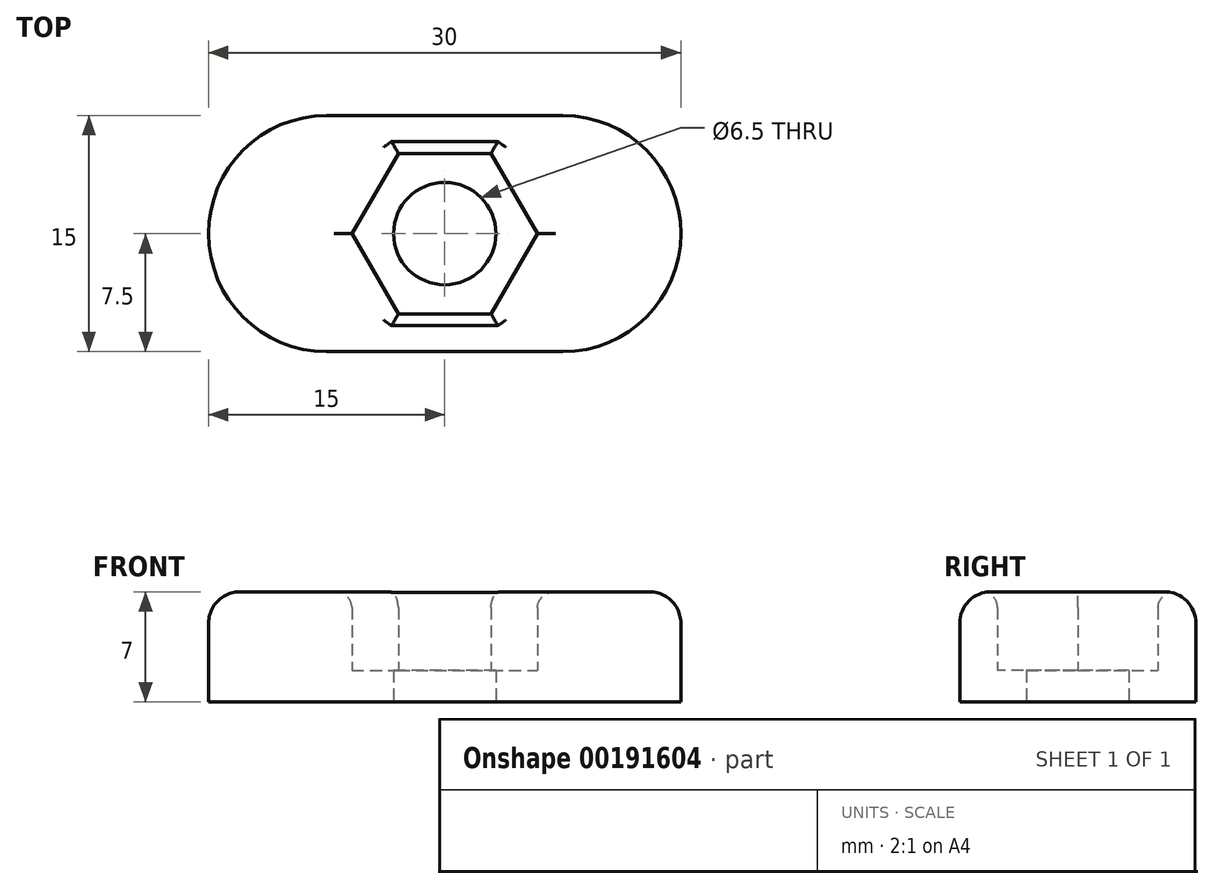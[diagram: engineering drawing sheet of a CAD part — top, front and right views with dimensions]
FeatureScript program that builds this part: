
annotation { "Feature Type Name" : "Feature", "Feature Type Description" : "" }
export const myFeature = defineFeature(function(context is Context, id is Id, definition is map)
    precondition{}
    {
        {
            var Q0;
            Q0=qCreatedBy(makeId("Top.planeOp"),FACE);
            var sketch = newSketch(context, id + "F0", { "sketchPlane" : qUnion([Q0])});
            skCircle(sketch, "E0.cCircle", {"center": v(0, 0) * mm, "radius": 5.1 * mm, "construction": true});
            skLineSegment(sketch, "E0.0", {"start": v(-2.94, 5.1) * mm, "end": v(2.94, 5.1) * mm});
            skLineSegment(sketch, "E0.1", {"start": v(2.94, 5.1) * mm, "end": v(5.89, 0) * mm});
            skLineSegment(sketch, "E0.2", {"start": v(5.89, 0) * mm, "end": v(2.94, -5.1) * mm});
            skLineSegment(sketch, "E0.3", {"start": v(2.94, -5.1) * mm, "end": v(-2.94, -5.1) * mm});
            skLineSegment(sketch, "E0.4", {"start": v(-2.94, -5.1) * mm, "end": v(-5.89, 0) * mm});
            skLineSegment(sketch, "E0.5", {"start": v(-5.89, 0) * mm, "end": v(-2.94, 5.1) * mm});
            skPoint(sketch, "E0.0.midPoint", {"position": v(0, 5.1) * mm});
            skLineSegment(sketch, "E1.bottom", {"start": v(-15, 7.5) * mm, "end": v(15, 7.5) * mm});
            skLineSegment(sketch, "E1.top", {"start": v(-15, -7.5) * mm, "end": v(15, -7.5) * mm});
            skLineSegment(sketch, "E1.left", {"start": v(-15, 7.5) * mm, "end": v(-15, -7.5) * mm});
            skLineSegment(sketch, "E1.right", {"start": v(15, 7.5) * mm, "end": v(15, -7.5) * mm});
            skCircle(sketch, "E2", {"center": v(0, 0) * mm, "radius": 3.25 * mm});
            skSolve(sketch);
        }
        {
            var Q0;
            Q0=makeQuery(id+"F0.imprint","IMPRINT",FACE,{"disambiguationData":[TD([[makeQuery(id+"F0.imprint","IMPRINT",EDGE,{"derivedFrom":sQuery(id+"F0.wireOp",EDGE,"E0.0")}),1.0]])]});
            extrude(context, id + "F1", {"entities" : qUnion([Q0]), "depth" : 7 * mm});
        }
        {
            var Q0;
            Q0=makeQuery(id+"F1.opExtrude","SWEPT_EDGE",EDGE,{"disambiguationData":[OSD([sQuery(id+"F0.wireOp",EDGE,"E1.top"),sQuery(id+"F0.wireOp",EDGE,"E1.left")])]});
            var Q1;
            Q1=makeQuery(id+"F1.opExtrude","SWEPT_EDGE",EDGE,{"disambiguationData":[OSD([sQuery(id+"F0.wireOp",EDGE,"E1.bottom"),sQuery(id+"F0.wireOp",EDGE,"E1.right")])]});
            var Q2;
            Q2=makeQuery(id+"F1.opExtrude","SWEPT_EDGE",EDGE,{"disambiguationData":[OSD([sQuery(id+"F0.wireOp",EDGE,"E1.bottom"),sQuery(id+"F0.wireOp",EDGE,"E1.left")])]});
            var Q3;
            Q3=makeQuery(id+"F1.opExtrude","SWEPT_EDGE",EDGE,{"disambiguationData":[OSD([sQuery(id+"F0.wireOp",EDGE,"E1.top"),sQuery(id+"F0.wireOp",EDGE,"E1.right")])]});
            fillet(context, id + "F2", {"entities" : qUnion([Q0, Q1, Q2, Q3]), "radius" : 7.5 * mm, "tangentPropagation" : true, "allowEdgeOverflow" : false});
        }
        {
            var Q0;
            {var subQ0=sQuery(id+"F0.wireOp",EDGE,"E1.right");var subQ1=sQuery(id+"F0.wireOp",EDGE,"E1.bottom");Q0=makeQuery(id+"F2.opFillet","BLEND_EDGE",EDGE,{"blendedFrom":[makeQuery(id+"F1.opExtrude","SWEPT_EDGE",EDGE,{"disambiguationData":[OSD([subQ1,subQ0])]}),makeQuery(id+"F1.opExtrude","CAP_FACE",FACE,{"disambiguationData":[OSD([sQuery(id+"F0.wireOp",EDGE,"E0.0"),sQuery(id+"F0.wireOp",EDGE,"E0.1"),sQuery(id+"F0.wireOp",EDGE,"E0.2"),sQuery(id+"F0.wireOp",EDGE,"E0.3"),sQuery(id+"F0.wireOp",EDGE,"E0.4"),sQuery(id+"F0.wireOp",EDGE,"E0.5"),subQ1,sQuery(id+"F0.wireOp",EDGE,"E1.top"),sQuery(id+"F0.wireOp",EDGE,"E1.left"),subQ0])],"isStart":false})],"blendedInto":[makeQuery(id+"F1.opExtrude","CAP_FACE",FACE,{"disambiguationData":[OSD([sQuery(id+"F0.wireOp",EDGE,"E0.0"),sQuery(id+"F0.wireOp",EDGE,"E0.1"),sQuery(id+"F0.wireOp",EDGE,"E0.2"),sQuery(id+"F0.wireOp",EDGE,"E0.3"),sQuery(id+"F0.wireOp",EDGE,"E0.4"),sQuery(id+"F0.wireOp",EDGE,"E0.5"),subQ1,sQuery(id+"F0.wireOp",EDGE,"E1.top"),sQuery(id+"F0.wireOp",EDGE,"E1.left"),subQ0])],"isStart":false})]});}
            fillet(context, id + "F3", {"entities" : qUnion([Q0]), "radius" : 2 * mm, "tangentPropagation" : true, "allowEdgeOverflow" : false});
        }
        {
            var Q0;
            Q0=makeQuery(id+"F1.opExtrude","CAP_EDGE",EDGE,{"disambiguationData":[OSD([sQuery(id+"F0.wireOp",EDGE,"E0.1")])],"isStart":false});
            var Q1;
            Q1=makeQuery(id+"F1.opExtrude","CAP_EDGE",EDGE,{"disambiguationData":[OSD([sQuery(id+"F0.wireOp",EDGE,"E0.2")])],"isStart":false});
            var Q2;
            Q2=makeQuery(id+"F1.opExtrude","CAP_EDGE",EDGE,{"disambiguationData":[OSD([sQuery(id+"F0.wireOp",EDGE,"E0.0")])],"isStart":false});
            var Q3;
            Q3=makeQuery(id+"F1.opExtrude","CAP_EDGE",EDGE,{"disambiguationData":[OSD([sQuery(id+"F0.wireOp",EDGE,"E0.5")])],"isStart":false});
            var Q4;
            Q4=makeQuery(id+"F1.opExtrude","CAP_EDGE",EDGE,{"disambiguationData":[OSD([sQuery(id+"F0.wireOp",EDGE,"E0.4")])],"isStart":false});
            var Q5;
            Q5=makeQuery(id+"F1.opExtrude","CAP_EDGE",EDGE,{"disambiguationData":[OSD([sQuery(id+"F0.wireOp",EDGE,"E0.3")])],"isStart":false});
            fillet(context, id + "F4", {"entities" : qUnion([Q0, Q1, Q2, Q3, Q4, Q5]), "radius" : 1 * mm, "tangentPropagation" : true, "allowEdgeOverflow" : false});
        }
        {
            var Q0;
            Q0=makeQuery(id+"F0.imprint","IMPRINT",FACE,{"disambiguationData":[TD([[makeQuery(id+"F0.imprint","IMPRINT",EDGE,{"derivedFrom":sQuery(id+"F0.wireOp",EDGE,"E0.0")}),-1.0]])]});
            extrude(context, id + "F5", {"entities" : qUnion([Q0]), "operationType" : NewBodyOperationType.ADD, "depth" : 2 * mm});
        }
    });
